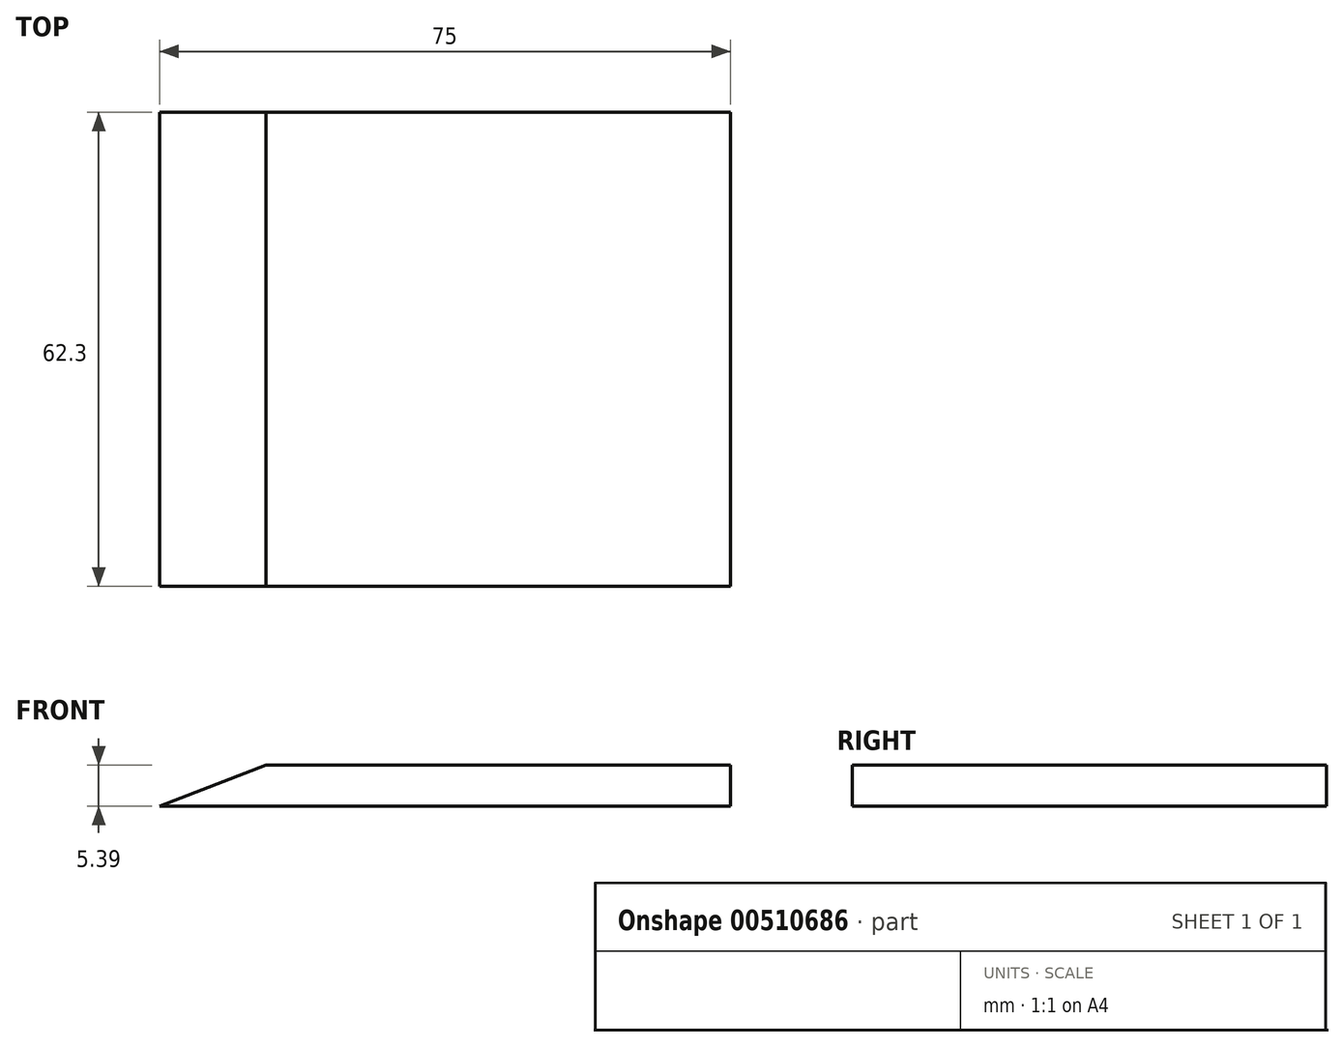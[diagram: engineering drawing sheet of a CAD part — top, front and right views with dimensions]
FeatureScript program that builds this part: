
annotation { "Feature Type Name" : "Feature", "Feature Type Description" : "" }
export const myFeature = defineFeature(function(context is Context, id is Id, definition is map)
    precondition{}
    {
        {
            var Q0;
            Q0=qCreatedBy(makeId("Front.planeOp"),FACE);
            var sketch = newSketch(context, id + "F0", { "sketchPlane" : qUnion([Q0])});
            skLineSegment(sketch, "E0.bottom", {"start": v(-75, 0) * mm, "end": v(0, 0) * mm});
            skLineSegment(sketch, "E0.top", {"start": v(-61, 5.39) * mm, "end": v(0, 5.39) * mm});
            skLineSegment(sketch, "E0.left", {"start": v(-75, 0) * mm, "end": v(-75, 0) * mm});
            skLineSegment(sketch, "E0.right", {"start": v(0, 0) * mm, "end": v(0, 5.39) * mm});
            skLineSegment(sketch, "E1", {"start": v(-75, 0) * mm, "end": v(-61, 5.39) * mm});
            skSolve(sketch);
        }
        {
            var Q0;
            Q0 = qSketchRegion(id + "F0", true);
            extrude(context, id + "F1", {"entities" : qUnion([Q0]), "depth" : 62.3 * mm, "offsetDistance" : 25 * mm});
        }
    });
